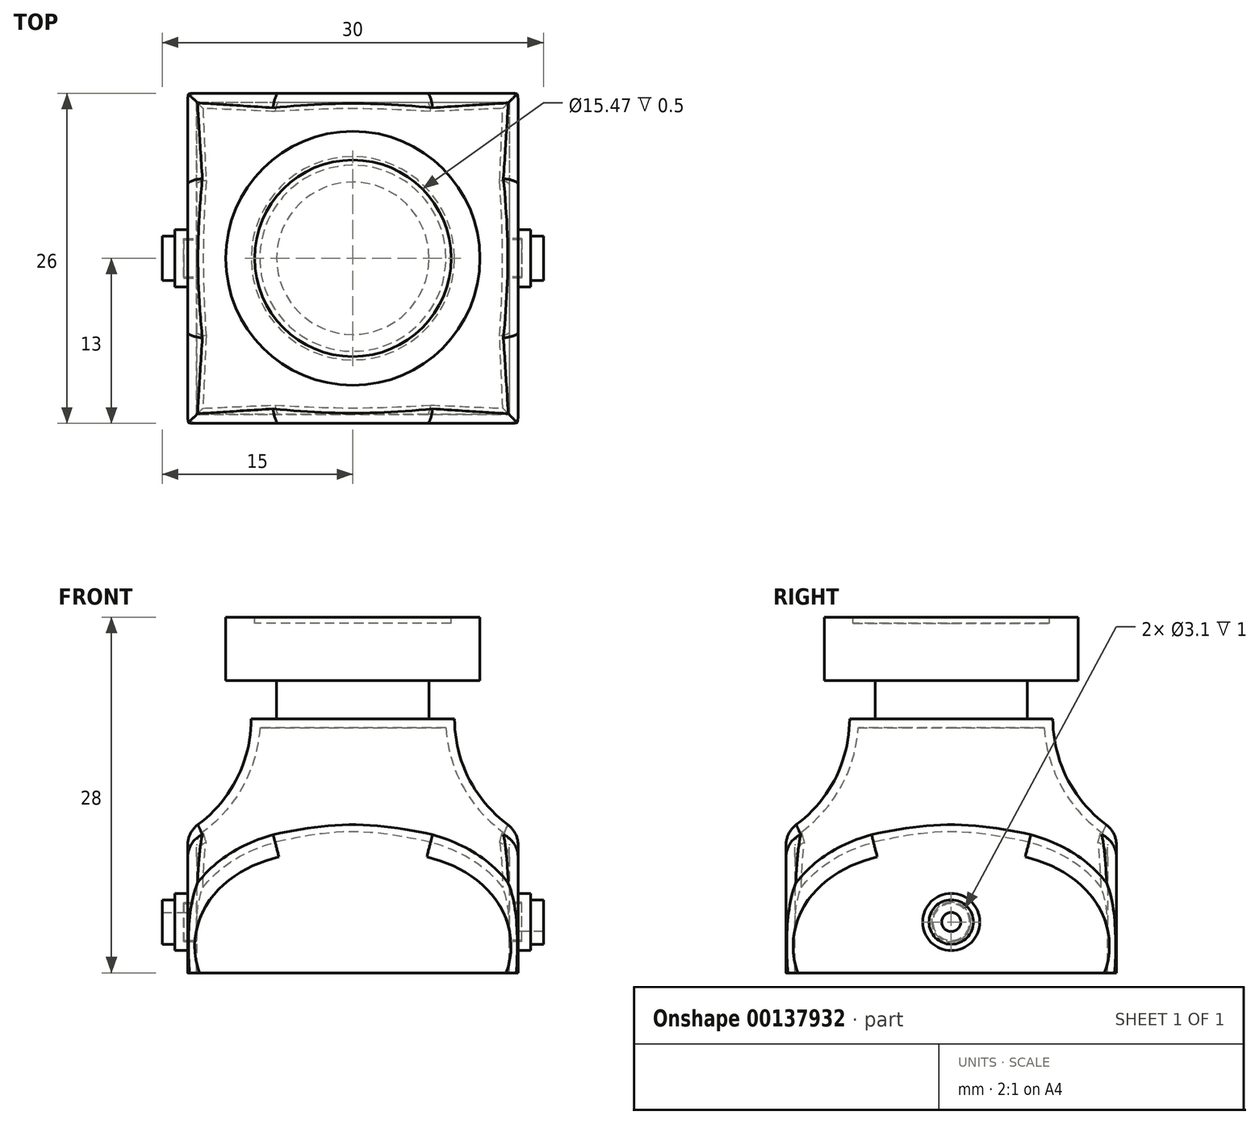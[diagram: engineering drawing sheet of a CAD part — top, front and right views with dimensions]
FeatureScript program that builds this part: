
annotation { "Feature Type Name" : "Feature", "Feature Type Description" : "" }
export const myFeature = defineFeature(function(context is Context, id is Id, definition is map)
    precondition{}
    {
        {
            var Q0;
            Q0=qCreatedBy(makeId("Top.planeOp"),FACE);
            var sketch = newSketch(context, id + "F0", { "sketchPlane" : qUnion([Q0])});
            skLineSegment(sketch, "E0.bottom", {"start": v(13, -13) * mm, "end": v(-13, -13) * mm, "construction": true});
            skLineSegment(sketch, "E0.top", {"start": v(13, 13) * mm, "end": v(-13, 13) * mm, "construction": true});
            skLineSegment(sketch, "E0.left", {"start": v(13, -13) * mm, "end": v(13, 13) * mm, "construction": true});
            skLineSegment(sketch, "E0.right", {"start": v(-13, -13) * mm, "end": v(-13, 13) * mm, "construction": true});
            skPoint(sketch, "E0.middle", {"position": v(0, 0) * mm});
            skCircle(sketch, "E1", {"center": v(0, 0) * mm, "radius": 18.38 * mm});
            skLineSegment(sketch, "E2", {"start": v(0, 0) * mm, "end": v(18.38, 0) * mm, "construction": true});
            skSolve(sketch);
        }
        {
            var Q0;
            Q0=qCreatedBy(makeId("Front.planeOp"),FACE);
            var sketch = newSketch(context, id + "F1", { "sketchPlane" : qUnion([Q0])});
            skLineSegment(sketch, "E3", {"start": v(0, 0) * mm, "end": v(0, 20) * mm, "construction": true});
            skLineSegment(sketch, "E4", {"start": v(0, 20) * mm, "end": v(8, 20) * mm});
            skPoint(sketch, "E5.0", {"position": v(18.38, 0) * mm});
            skPoint(sketch, "E6", {"position": v(4.38, 0) * mm});
            skLineSegment(sketch, "E7", {"start": v(18.38, 0) * mm, "end": v(18.38, 20) * mm, "construction": true});
            skArc(sketch, "E8", {"start": v(8, 20) * mm, "mid": v(9.45, 14.7) * mm, "end": v(13.4, 10.89) * mm});
            skPoint(sketch, "E9", {"position": v(13.4, 10.89) * mm});
            skArc(sketch, "E10", {"start": v(13.4, 10.89) * mm, "mid": v(17.7, 6.27) * mm, "end": v(18.38, 0) * mm});
            skLineSegment(sketch, "E11", {"start": v(18.38, 0) * mm, "end": v(0, 0) * mm});
            skLineSegment(sketch, "E12", {"start": v(0, 20) * mm, "end": v(0, 0) * mm});
            skLineSegment(sketch, "E13", {"start": v(0, 0) * mm, "end": v(0, 39.48) * mm, "construction": true});
            skPoint(sketch, "E13.endSnap0", {"position": v(0, 10) * mm});
            skSolve(sketch);
        }
        {
            var Q0;
            Q0 = qSketchRegion(id + "F1", true);
            var Q1;
            Q1=sQuery(id+"F1.wireOp",EDGE,"E13");
            revolve(context, id + "F2", {"entities" : qUnion([Q0]), "axis" : qUnion([Q1]), "revolveType" : RevolveType.FULL});
        }
        {
            var Q0;
            Q0=makeQuery(id+"F0.imprint","IMPRINT",FACE,{"disambiguationData":[TD([[makeQuery(id+"F0.imprint","IMPRINT",EDGE,{"derivedFrom":sQuery(id+"F0.wireOp",EDGE,"E1")}),1.0]])]});
            var sketch = newSketch(context, id + "F3", { "sketchPlane" : qUnion([Q0])});
            skLineSegment(sketch, "E14.bottom", {"start": v(-13, 13) * mm, "end": v(13, 13) * mm});
            skLineSegment(sketch, "E14.top", {"start": v(-13, -13) * mm, "end": v(13, -13) * mm});
            skLineSegment(sketch, "E14.left", {"start": v(-13, 13) * mm, "end": v(-13, -13) * mm});
            skLineSegment(sketch, "E14.right", {"start": v(13, 13) * mm, "end": v(13, -13) * mm});
            skPoint(sketch, "E14.middle", {"position": v(0, 0) * mm});
            skLineSegment(sketch, "E15.bottom", {"start": v(-30, 30) * mm, "end": v(30, 30) * mm});
            skLineSegment(sketch, "E15.top", {"start": v(-30, -30) * mm, "end": v(30, -30) * mm});
            skLineSegment(sketch, "E15.left", {"start": v(-30, 30) * mm, "end": v(-30, -30) * mm});
            skLineSegment(sketch, "E15.right", {"start": v(30, 30) * mm, "end": v(30, -30) * mm});
            skSolve(sketch);
        }
        {
            var Q0;
            Q0 = qSketchRegion(id + "F3", true);
            extrude(context, id + "F4", {"entities" : qUnion([Q0]), "operationType" : NewBodyOperationType.REMOVE, "endBound" : BoundingType.THROUGH_ALL, "depth" : 25 * mm});
        }
        {
            var Q0;
            Q0=makeQuery(id+"F4.boolean.opBoolean","INTERSECT",EDGE,{"disambiguationData":[OD(0.0)],"derivedFrom":[makeQuery(id+"F2.opRevolve","SWEPT_FACE",FACE,{"disambiguationData":[OSD([sQuery(id+"F1.wireOp",EDGE,"E10")])]}),makeQuery(id+"F4.opExtrude","SWEPT_FACE",FACE,{"disambiguationData":[OSD([sQuery(id+"F3.wireOp",EDGE,"E14.right")])]})]});
            var Q1;
            Q1=makeQuery(id+"F4.boolean.opBoolean","INTERSECT",EDGE,{"disambiguationData":[OD(1.0)],"derivedFrom":[makeQuery(id+"F2.opRevolve","SWEPT_FACE",FACE,{"disambiguationData":[OSD([sQuery(id+"F1.wireOp",EDGE,"E10")])]}),makeQuery(id+"F4.opExtrude","SWEPT_FACE",FACE,{"disambiguationData":[OSD([sQuery(id+"F3.wireOp",EDGE,"E14.bottom")])]})]});
            var Q2;
            Q2=makeQuery(id+"F4.boolean.opBoolean","INTERSECT",EDGE,{"disambiguationData":[OD(0.0)],"derivedFrom":[makeQuery(id+"F2.opRevolve","SWEPT_FACE",FACE,{"disambiguationData":[OSD([sQuery(id+"F1.wireOp",EDGE,"E10")])]}),makeQuery(id+"F4.opExtrude","SWEPT_FACE",FACE,{"disambiguationData":[OSD([sQuery(id+"F3.wireOp",EDGE,"E14.left")])]})]});
            var Q3;
            Q3=makeQuery(id+"F4.boolean.opBoolean","INTERSECT",EDGE,{"disambiguationData":[OD(0.0)],"derivedFrom":[makeQuery(id+"F2.opRevolve","SWEPT_FACE",FACE,{"disambiguationData":[OSD([sQuery(id+"F1.wireOp",EDGE,"E10")])]}),makeQuery(id+"F4.opExtrude","SWEPT_FACE",FACE,{"disambiguationData":[OSD([sQuery(id+"F3.wireOp",EDGE,"E14.top")])]})]});
            fillet(context, id + "F5", {"entities" : qUnion([Q0, Q1, Q2, Q3]), "radius" : 2 * mm, "tangentPropagation" : true, "allowEdgeOverflow" : false});
        }
        {
            var Q0;
            Q0=makeQuery(id+"F4.boolean.opBoolean","COPY",FACE,{"derivedFrom":makeQuery(id+"F4.opExtrude","SWEPT_FACE",FACE,{"disambiguationData":[OSD([sQuery(id+"F3.wireOp",EDGE,"E14.left")])]})});
            var sketch = newSketch(context, id + "F6", { "sketchPlane" : qUnion([Q0])});
            skLineSegment(sketch, "E16", {"start": v(0, 0) * mm, "end": v(0, 4) * mm, "construction": true});
            skCircle(sketch, "E17", {"center": v(0, 4) * mm, "radius": 2.25 * mm});
            skCircle(sketch, "E18", {"center": v(0, 4) * mm, "radius": 1.75 * mm});
            skCircle(sketch, "E19", {"center": v(0, 4) * mm, "radius": 0.75 * mm});
            skSolve(sketch);
        }
        {
            var Q0;
            Q0=makeQuery(id+"F6.imprint","IMPRINT",FACE,{"disambiguationData":[TD([[makeQuery(id+"F6.imprint","IMPRINT",EDGE,{"derivedFrom":sQuery(id+"F6.wireOp",EDGE,"E17")}),1.0]])]});
            var Q1;
            Q1=sQuery(id+"F6.wireOp",EDGE,"E17");
            extrude(context, id + "F7", {"entities" : qUnion([Q0]), "operationType" : NewBodyOperationType.ADD, "surfaceEntities" : qUnion([Q1]), "depth" : 1 * mm});
        }
        {
            var Q0;
            Q0=makeQuery(id+"F7.boolean.opBoolean","SPLIT",FACE,{"disambiguationData":[TD([makeQuery(id+"F7.opExtrude","SWEPT_FACE",FACE,{"disambiguationData":[OSD([sQuery(id+"F6.wireOp",EDGE,"E18")])]})])],"derivedFrom":makeQuery(id+"F4.boolean.opBoolean","COPY",FACE,{"derivedFrom":makeQuery(id+"F4.opExtrude","SWEPT_FACE",FACE,{"disambiguationData":[OSD([sQuery(id+"F3.wireOp",EDGE,"E14.left")])]})})});
            var Q1;
            Q1=makeQuery(id+"F6.imprint","IMPRINT",FACE,{"disambiguationData":[TD([[makeQuery(id+"F6.imprint","IMPRINT",EDGE,{"derivedFrom":sQuery(id+"F6.wireOp",EDGE,"E18")}),1.0]])]});
            var Q2;
            Q2=sQuery(id+"F6.wireOp",EDGE,"E18");
            var Q3;
            Q3=sQuery(id+"F6.wireOp",EDGE,"E19");
            extrude(context, id + "F8", {"entities" : qUnion([Q0, Q1]), "operationType" : NewBodyOperationType.ADD, "surfaceEntities" : qUnion([Q2, Q3]), "depth" : 2 * mm});
        }
        {
            var Q0;
            Q0=makeQuery(id+"F6.imprint","IMPRINT",FACE,{"disambiguationData":[TD([[makeQuery(id+"F6.imprint","IMPRINT",EDGE,{"derivedFrom":sQuery(id+"F6.wireOp",EDGE,"E19")}),1.0]])]});
            extrude(context, id + "F9", {"entities" : qUnion([Q0]), "operationType" : NewBodyOperationType.REMOVE, "depth" : 25 * mm});
        }
        {
            var Q0;
            Q0=makeQuery(id+"F2.opRevolve","SWEPT_BODY",BODY,{"disambiguationData":[OSD([sQuery(id+"F1.wireOp",EDGE,"E4"),sQuery(id+"F1.wireOp",EDGE,"E8"),sQuery(id+"F1.wireOp",EDGE,"E10"),sQuery(id+"F1.wireOp",EDGE,"E11"),sQuery(id+"F1.wireOp",EDGE,"E12")])]});
            var Q1;
            Q1=qCreatedBy(makeId("Right.planeOp"),FACE);
            mirror(context, id + "F10", {"operationType" : NewBodyOperationType.ADD, "entities" : qUnion([Q0]), "mirrorPlane" : qUnion([Q1])});
        }
        {
            var Q0;
            Q0=makeQuery(id+"F2.opRevolve","SWEPT_FACE",FACE,{"disambiguationData":[OSD([sQuery(id+"F1.wireOp",EDGE,"E4")])]});
            var sketch = newSketch(context, id + "F11", { "sketchPlane" : qUnion([Q0])});
            skCircle(sketch, "E20", {"center": v(0, 0) * mm, "radius": 6 * mm});
            skSolve(sketch);
        }
        {
            var Q0;
            Q0=makeQuery(id+"F11.imprint","IMPRINT",FACE,{"disambiguationData":[TD([[makeQuery(id+"F11.imprint","IMPRINT",EDGE,{"derivedFrom":sQuery(id+"F11.wireOp",EDGE,"E20")}),1.0]])]});
            var Q1;
            Q1=sQuery(id+"F11.wireOp",EDGE,"E20");
            extrude(context, id + "F12", {"entities" : qUnion([Q0]), "surfaceEntities" : qUnion([Q1]), "depth" : 3 * mm});
        }
        {
            var Q0;
            Q0=makeQuery(id+"F12.opExtrude","CAP_FACE",FACE,{"disambiguationData":[OSD([sQuery(id+"F11.wireOp",EDGE,"E20")])],"isStart":false});
            var sketch = newSketch(context, id + "F13", { "sketchPlane" : qUnion([Q0])});
            skCircle(sketch, "E21", {"center": v(0, 0) * mm, "radius": 10 * mm});
            skSolve(sketch);
        }
        {
            var Q0;
            Q0 = qSketchRegion(id + "F13", true);
            extrude(context, id + "F14", {"entities" : qUnion([Q0]), "operationType" : NewBodyOperationType.ADD, "depth" : 5 * mm});
        }
        {
            var Q0;
            Q0=makeQuery(id+"F14.opExtrude","CAP_FACE",FACE,{"disambiguationData":[OSD([sQuery(id+"F13.wireOp",EDGE,"E21")])],"isStart":false});
            var sketch = newSketch(context, id + "F15", { "sketchPlane" : qUnion([Q0])});
            skCircle(sketch, "E22", {"center": v(0, 0) * mm, "radius": 7.73 * mm});
            skSolve(sketch);
        }
        {
            var Q0;
            Q0 = qSketchRegion(id + "F15", true);
            extrude(context, id + "F16", {"entities" : qUnion([Q0]), "operationType" : NewBodyOperationType.REMOVE, "oppositeDirection" : true, "depth" : .5 * mm});
        }
        {
            var Q0;
            Q0=makeQuery(id+"F2.opRevolve","SWEPT_FACE",FACE,{"disambiguationData":[OSD([sQuery(id+"F1.wireOp",EDGE,"E11")])]});
            shell(context, id + "F17", {"entities" : qUnion([Q0]), "thickness" : .7 * mm});
        }
    });
